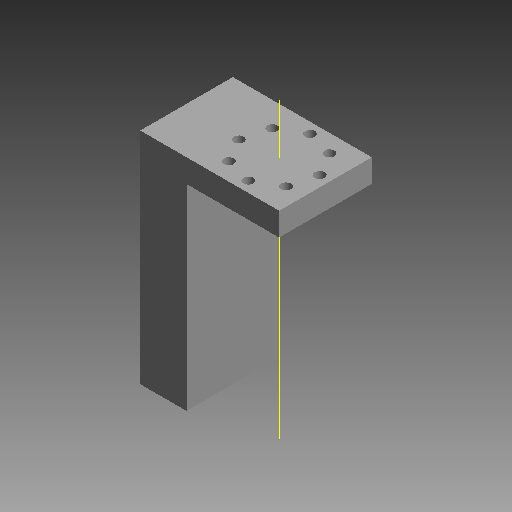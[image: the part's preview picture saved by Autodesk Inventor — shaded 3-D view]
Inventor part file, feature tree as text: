
AUTODESK INVENTOR PART (.ipt)
format: ipt  version: 2019 (Build 230136000, 136)  size: 84,992 bytes
history: native  units: mm (DEFAULTED — no unit token found)
features: other x4, sketch x2
ambient origin geometry x8: Origin, YZ Plane, XZ Plane, XY Plane, X Axis, Y Axis, Z Axis, Center Point
bodies: Solid1 (feature_tree)
feature tree (6):
  other  "wheel arm stand off.ipt"
  other  "Solid3::wheel arm stand off.ipt"
  other  "TaggingFeature1"
  sketch  "Sketch4"  dims[d0=10.0mm]
  sketch  "Sketch5"
  other  "Work Axis1"
